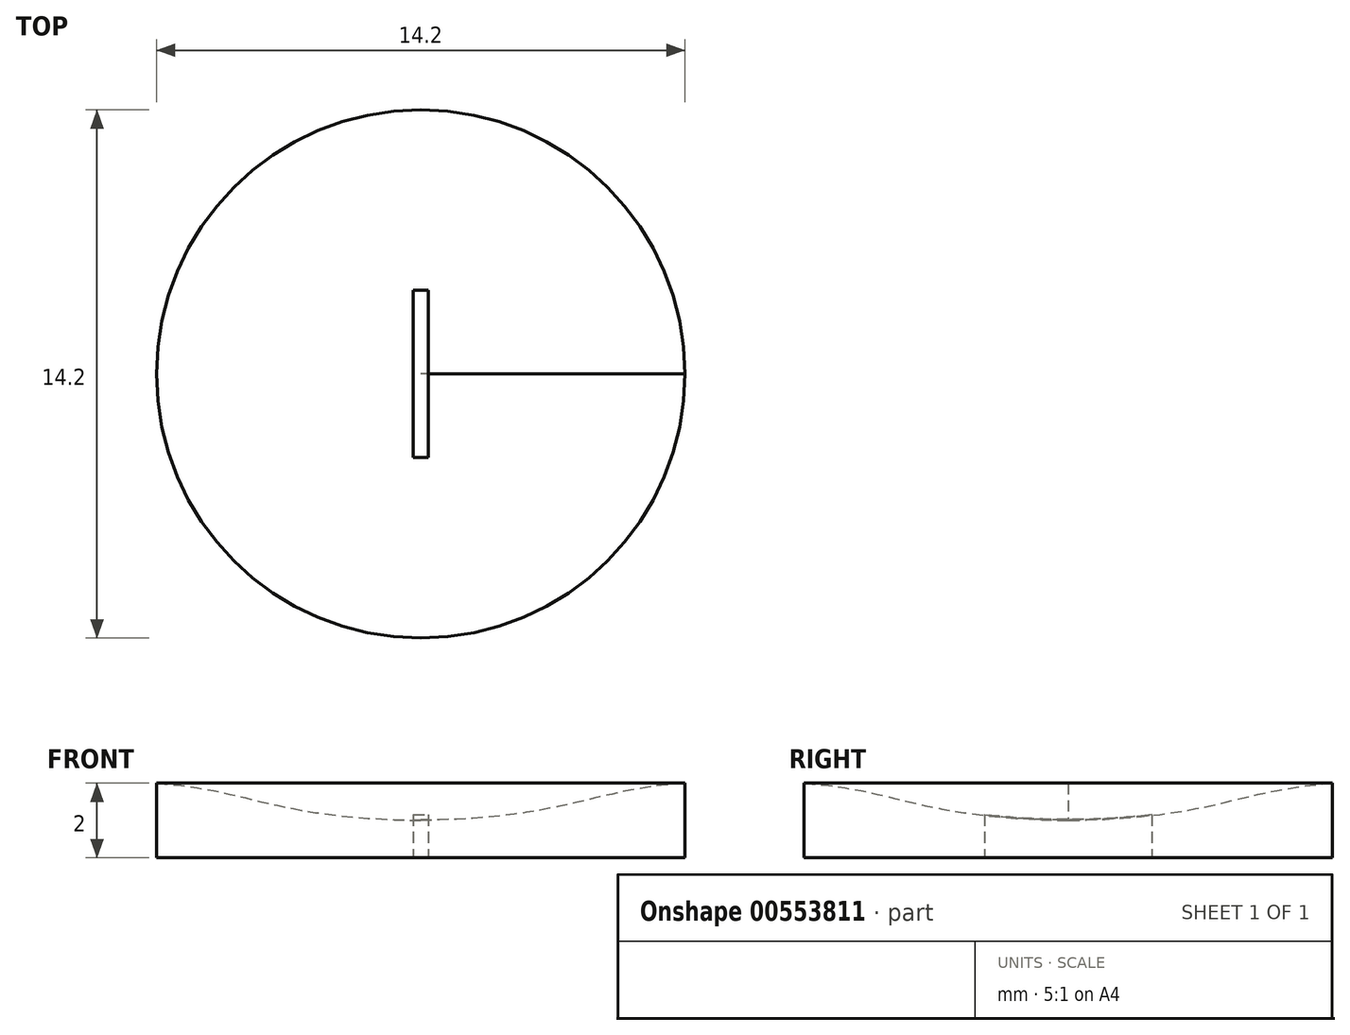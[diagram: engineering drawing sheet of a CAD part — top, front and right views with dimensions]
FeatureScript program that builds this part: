
annotation { "Feature Type Name" : "Feature", "Feature Type Description" : "" }
export const myFeature = defineFeature(function(context is Context, id is Id, definition is map)
    precondition{}
    {
        {
            var Q0;
            Q0=qCreatedBy(makeId("Front.planeOp"),FACE);
            var sketch = newSketch(context, id + "F0", { "sketchPlane" : qUnion([Q0])});
            skLineSegment(sketch, "E0", {"start": v(0, 0) * mm, "end": v(7.1, 0) * mm});
            skLineSegment(sketch, "E1", {"start": v(7.1, 0) * mm, "end": v(7.1, 2) * mm});
            skLineSegment(sketch, "E2", {"start": v(0, 1) * mm, "end": v(0, 0) * mm});
            skFitSpline(sketch, "E3", {"points": [v(7.1, 2) * mm, v(0, 1) * mm], "startDerivative": vector(-7.89, -0.57) * mm, "endDerivative": vector(-12, -0.18) * mm});
            skPoint(sketch, "E4.orphan", {"position": v(0, 2) * mm});
            skSolve(sketch);
        }
        {
            var Q0;
            Q0=makeQuery(id+"F0.imprint","IMPRINT",FACE,{"disambiguationData":[TD([[makeQuery(id+"F0.imprint","IMPRINT",EDGE,{"derivedFrom":sQuery(id+"F0.wireOp",EDGE,"E0")}),1.0]])]});
            var Q1;
            Q1=sQuery(id+"F0.wireOp",EDGE,"E2");
            revolve(context, id + "F1", {"entities" : qUnion([Q0]), "axis" : qUnion([Q1]), "revolveType" : RevolveType.FULL});
        }
        {
            var Q0;
            Q0=makeQuery(id+"F1.opRevolve","SWEPT_FACE",FACE,{"disambiguationData":[OSD([sQuery(id+"F0.wireOp",EDGE,"E0")])]});
            var sketch = newSketch(context, id + "F2", { "sketchPlane" : qUnion([Q0])});
            skLineSegment(sketch, "E5.bottom", {"start": v(0.2, -2.25) * mm, "end": v(-0.2, -2.25) * mm});
            skLineSegment(sketch, "E5.top", {"start": v(0.2, 2.25) * mm, "end": v(-0.2, 2.25) * mm});
            skLineSegment(sketch, "E5.left", {"start": v(0.2, -2.25) * mm, "end": v(0.2, -0.2) * mm});
            skLineSegment(sketch, "E5.right", {"start": v(-0.2, -2.25) * mm, "end": v(-0.2, -0.2) * mm});
            skPoint(sketch, "E5.middle", {"position": v(0, 0) * mm});
            skLineSegment(sketch, "E6.trimOffspring", {"start": v(-0.2, 0.2) * mm, "end": v(-0.2, 2.25) * mm});
            skLineSegment(sketch, "E7.trimOffspring", {"start": v(0.2, 0.2) * mm, "end": v(0.2, 2.25) * mm});
            skLineSegment(sketch, "E8", {"start": v(0.2, 0.2) * mm, "end": v(0.2, -0.2) * mm});
            skLineSegment(sketch, "E9", {"start": v(-0.2, 0.2) * mm, "end": v(-0.2, -0.2) * mm});
            skSolve(sketch);
        }
        {
            var Q0;
            Q0=makeQuery(id+"F2.imprint","IMPRINT",FACE,{"disambiguationData":[TD([[makeQuery(id+"F2.imprint","IMPRINT",EDGE,{"derivedFrom":sQuery(id+"F2.wireOp",EDGE,"E5.bottom")}),-1.0]])]});
            extrude(context, id + "F3", {"entities" : qUnion([Q0]), "endBound" : BoundingType.UP_TO_NEXT, "oppositeDirection" : true, "depth" : 25 * mm, "hasOffset" : true, "offsetDistance" : 0.02 * mm, "offsetOppositeDirection" : true});
        }
    });
